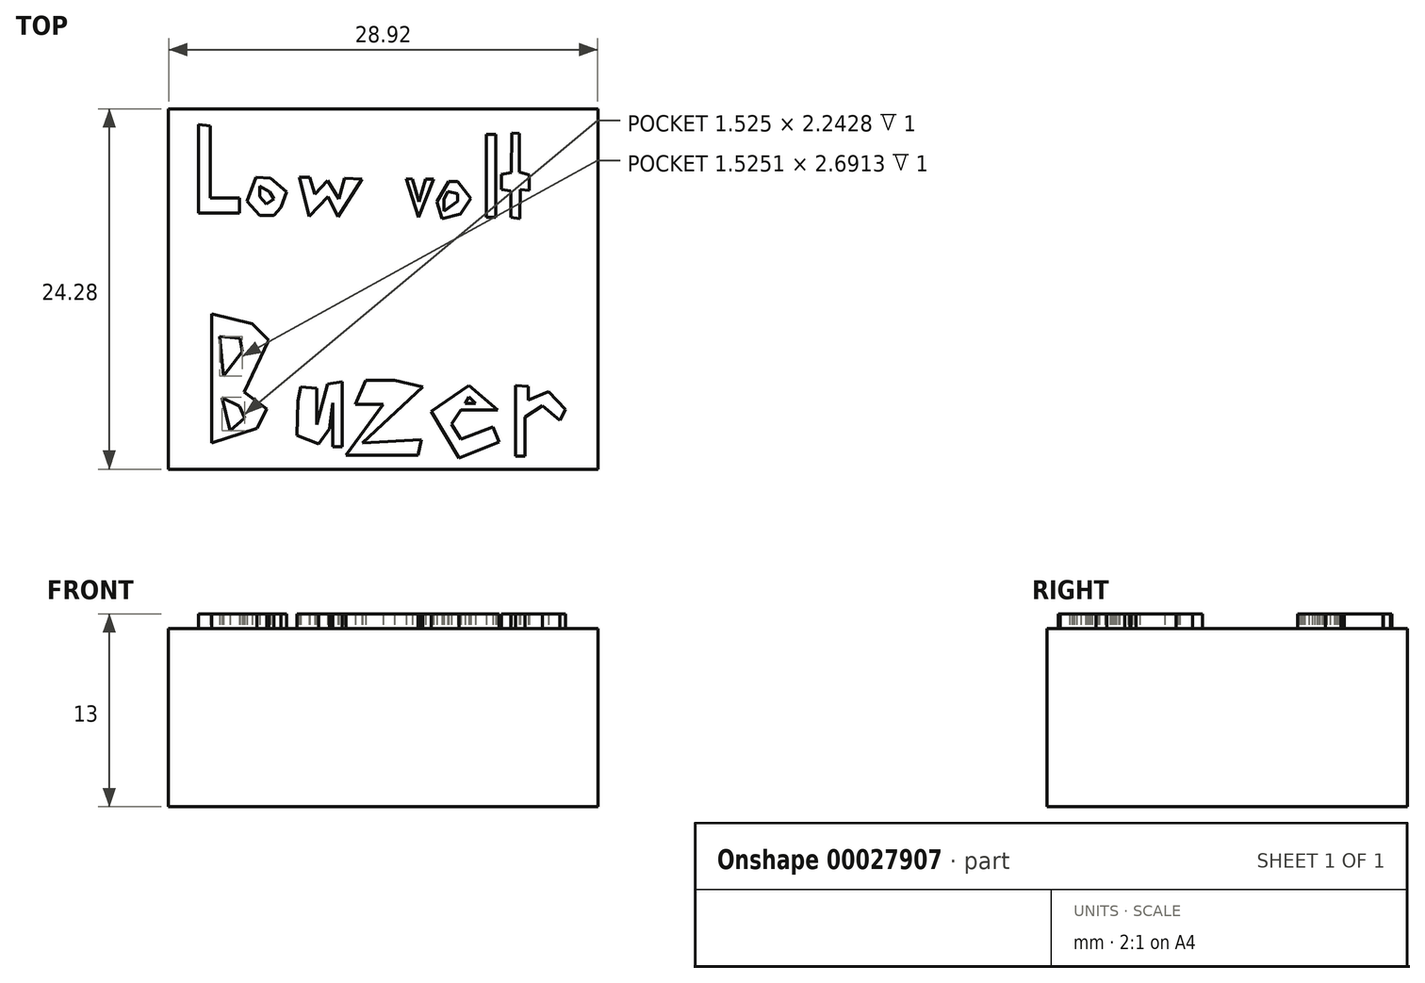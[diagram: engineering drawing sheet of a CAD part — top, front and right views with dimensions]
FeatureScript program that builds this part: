
annotation { "Feature Type Name" : "Feature", "Feature Type Description" : "" }
export const myFeature = defineFeature(function(context is Context, id is Id, definition is map)
    precondition{}
    {
        {
            var Q0;
            Q0=qCreatedBy(makeId("Top.planeOp"),FACE);
            var sketch = newSketch(context, id + "F0", { "sketchPlane" : qUnion([Q0])});
            skLineSegment(sketch, "E0.rect.bottom", {"start": v(14.47, 12.14) * mm, "end": v(-14.46, 12.14) * mm});
            skLineSegment(sketch, "E0.rect.top", {"start": v(14.47, -12.14) * mm, "end": v(-14.46, -12.14) * mm});
            skLineSegment(sketch, "E0.rect.left", {"start": v(14.47, 12.14) * mm, "end": v(14.47, -12.15) * mm});
            skLineSegment(sketch, "E0.rect.right", {"start": v(-14.46, 12.14) * mm, "end": v(-14.46, -12.14) * mm});
            skPoint(sketch, "E0.rect.middle", {"position": v(0, 0) * mm});
            skSolve(sketch);
        }
        {
            var Q0;
            Q0 = qSketchRegion(id + "F0", true);
            extrude(context, id + "F1", {"entities" : qUnion([Q0]), "depth" : 12 * mm});
        }
        {
            var Q0;
            Q0=makeQuery(id+"F1.opExtrude","CAP_FACE",FACE,{"disambiguationData":[OSD([sQuery(id+"F0.wireOp",EDGE,"E0.rect.bottom"),sQuery(id+"F0.wireOp",EDGE,"E0.rect.top"),sQuery(id+"F0.wireOp",EDGE,"E0.rect.left"),sQuery(id+"F0.wireOp",EDGE,"E0.rect.right")])],"isStart":false});
            var sketch = newSketch(context, id + "F2", { "sketchPlane" : qUnion([Q0])});
            skLineSegment(sketch, "E1", {"start": v(-12.45, 11.1) * mm, "end": v(-12.45, 5.12) * mm});
            skLineSegment(sketch, "E2", {"start": v(-12.45, 5.12) * mm, "end": v(-9.67, 5.12) * mm});
            skLineSegment(sketch, "E3", {"start": v(-9.67, 5.12) * mm, "end": v(-9.67, 6.14) * mm});
            skLineSegment(sketch, "E4", {"start": v(-9.67, 6.14) * mm, "end": v(-11.65, 6.14) * mm});
            skLineSegment(sketch, "E5", {"start": v(-11.65, 6.14) * mm, "end": v(-11.65, 11) * mm});
            skLineSegment(sketch, "E6", {"start": v(-11.65, 11) * mm, "end": v(-12.45, 11.1) * mm});
            skLineSegment(sketch, "E7", {"start": v(-8.56, 7.55) * mm, "end": v(-9.17, 5.9) * mm});
            skLineSegment(sketch, "E8", {"start": v(-9.17, 5.9) * mm, "end": v(-8.33, 4.96) * mm});
            skLineSegment(sketch, "E9", {"start": v(-8.33, 4.96) * mm, "end": v(-7.35, 4.96) * mm});
            skLineSegment(sketch, "E10", {"start": v(-7.35, 4.96) * mm, "end": v(-6.88, 5.5) * mm});
            skLineSegment(sketch, "E11", {"start": v(-6.88, 5.5) * mm, "end": v(-6.51, 6.54) * mm});
            skLineSegment(sketch, "E12", {"start": v(-6.51, 6.54) * mm, "end": v(-7.59, 7.48) * mm});
            skLineSegment(sketch, "E13", {"start": v(-7.59, 7.48) * mm, "end": v(-8.56, 7.55) * mm});
            skLineSegment(sketch, "E14", {"start": v(-8.33, 6.94) * mm, "end": v(-8.33, 6.24) * mm});
            skLineSegment(sketch, "E15", {"start": v(-8.33, 6.24) * mm, "end": v(-7.9, 5.73) * mm});
            skLineSegment(sketch, "E16", {"start": v(-7.9, 5.73) * mm, "end": v(-7.35, 6.07) * mm});
            skLineSegment(sketch, "E17", {"start": v(-7.35, 6.07) * mm, "end": v(-7.65, 6.55) * mm});
            skLineSegment(sketch, "E18", {"start": v(-7.65, 6.55) * mm, "end": v(-8.33, 6.94) * mm});
            skLineSegment(sketch, "E19", {"start": v(-5.64, 7.55) * mm, "end": v(-5, 4.9) * mm});
            skLineSegment(sketch, "E20", {"start": v(-5, 4.9) * mm, "end": v(-3.72, 6.24) * mm});
            skLineSegment(sketch, "E21", {"start": v(-3.72, 6.24) * mm, "end": v(-3.05, 4.86) * mm});
            skLineSegment(sketch, "E22", {"start": v(-3.05, 4.86) * mm, "end": v(-1.44, 7.41) * mm});
            skLineSegment(sketch, "E23", {"start": v(-1.44, 7.41) * mm, "end": v(-2.62, 7.48) * mm});
            skLineSegment(sketch, "E24", {"start": v(-2.62, 7.48) * mm, "end": v(-2.98, 6.07) * mm});
            skLineSegment(sketch, "E25", {"start": v(-2.98, 6.07) * mm, "end": v(-3.76, 7.31) * mm});
            skLineSegment(sketch, "E26", {"start": v(-3.76, 7.31) * mm, "end": v(-4.6, 6.4) * mm});
            skLineSegment(sketch, "E27", {"start": v(-4.6, 6.4) * mm, "end": v(-4.97, 7.55) * mm});
            skLineSegment(sketch, "E28", {"start": v(-4.97, 7.55) * mm, "end": v(-5.64, 7.55) * mm});
            skLineSegment(sketch, "E29", {"start": v(1.56, 7.45) * mm, "end": v(2.4, 4.84) * mm});
            skPoint(sketch, "E29.startSnap0", {"position": v(-2.03, 7.45) * mm});
            skLineSegment(sketch, "E30", {"start": v(2.4, 4.84) * mm, "end": v(3.38, 7.41) * mm});
            skLineSegment(sketch, "E31", {"start": v(3.38, 7.41) * mm, "end": v(2.84, 7.41) * mm});
            skLineSegment(sketch, "E32", {"start": v(2.84, 7.41) * mm, "end": v(2.43, 5.88) * mm});
            skLineSegment(sketch, "E33", {"start": v(2.43, 5.88) * mm, "end": v(1.98, 7.41) * mm});
            skLineSegment(sketch, "E34", {"start": v(1.98, 7.41) * mm, "end": v(1.56, 7.45) * mm});
            skLineSegment(sketch, "E35", {"start": v(4.4, 7.23) * mm, "end": v(3.62, 5.88) * mm});
            skLineSegment(sketch, "E36", {"start": v(3.62, 5.88) * mm, "end": v(3.98, 4.75) * mm});
            skLineSegment(sketch, "E37", {"start": v(3.98, 4.75) * mm, "end": v(5.2, 5.05) * mm});
            skLineSegment(sketch, "E38", {"start": v(5.2, 5.05) * mm, "end": v(5.9, 6.1) * mm});
            skLineSegment(sketch, "E39", {"start": v(5.9, 6.1) * mm, "end": v(5.03, 7.23) * mm});
            skLineSegment(sketch, "E40", {"start": v(5.03, 7.23) * mm, "end": v(4.4, 7.23) * mm});
            skLineSegment(sketch, "E41", {"start": v(4.34, 6.57) * mm, "end": v(4.1, 6.03) * mm});
            skLineSegment(sketch, "E42", {"start": v(4.1, 6.03) * mm, "end": v(4.1, 5.23) * mm});
            skLineSegment(sketch, "E43", {"start": v(4.1, 5.23) * mm, "end": v(5.03, 5.9) * mm});
            skLineSegment(sketch, "E44", {"start": v(5.03, 5.9) * mm, "end": v(5.03, 6.42) * mm});
            skLineSegment(sketch, "E45", {"start": v(5.03, 6.42) * mm, "end": v(4.34, 6.57) * mm});
            skLineSegment(sketch, "E46", {"start": v(6.95, 10.43) * mm, "end": v(6.95, 4.84) * mm});
            skLineSegment(sketch, "E47", {"start": v(6.95, 4.84) * mm, "end": v(7.57, 4.84) * mm});
            skLineSegment(sketch, "E48", {"start": v(7.57, 4.84) * mm, "end": v(7.57, 10.43) * mm});
            skLineSegment(sketch, "E49", {"start": v(7.57, 10.43) * mm, "end": v(6.95, 10.43) * mm});
            skLineSegment(sketch, "E50", {"start": v(8.6, 4.84) * mm, "end": v(8.6, 6.6) * mm});
            skLineSegment(sketch, "E51", {"start": v(8.6, 6.6) * mm, "end": v(7.96, 6.7) * mm});
            skLineSegment(sketch, "E52", {"start": v(7.96, 6.7) * mm, "end": v(7.96, 7.71) * mm});
            skLineSegment(sketch, "E53", {"start": v(7.96, 7.71) * mm, "end": v(8.65, 7.86) * mm});
            skLineSegment(sketch, "E54", {"start": v(8.65, 7.86) * mm, "end": v(8.68, 10.52) * mm});
            skLineSegment(sketch, "E55", {"start": v(8.68, 10.52) * mm, "end": v(9.2, 10.5) * mm});
            skLineSegment(sketch, "E56", {"start": v(9.2, 10.5) * mm, "end": v(9.16, 7.9) * mm});
            skLineSegment(sketch, "E57", {"start": v(9.16, 7.9) * mm, "end": v(9.85, 7.68) * mm});
            skLineSegment(sketch, "E58", {"start": v(9.85, 7.68) * mm, "end": v(9.85, 6.63) * mm});
            skLineSegment(sketch, "E59", {"start": v(9.85, 6.63) * mm, "end": v(9.25, 6.72) * mm});
            skLineSegment(sketch, "E60", {"start": v(9.25, 6.72) * mm, "end": v(9.22, 4.75) * mm});
            skLineSegment(sketch, "E61", {"start": v(9.22, 4.75) * mm, "end": v(8.6, 4.84) * mm});
            skLineSegment(sketch, "E62", {"start": v(-11.57, -1.66) * mm, "end": v(-11.57, -10.36) * mm});
            skLineSegment(sketch, "E63", {"start": v(-11.57, -10.36) * mm, "end": v(-8.52, -9.37) * mm});
            skLineSegment(sketch, "E64", {"start": v(-8.52, -9.37) * mm, "end": v(-7.85, -8.07) * mm});
            skLineSegment(sketch, "E65", {"start": v(-7.85, -8.07) * mm, "end": v(-9.37, -6.95) * mm});
            skLineSegment(sketch, "E66", {"start": v(-9.37, -6.95) * mm, "end": v(-7.71, -3.45) * mm});
            skLineSegment(sketch, "E67", {"start": v(-7.71, -3.45) * mm, "end": v(-8.83, -2.33) * mm});
            skLineSegment(sketch, "E68", {"start": v(-8.83, -2.33) * mm, "end": v(-11.57, -1.66) * mm});
            skLineSegment(sketch, "E69", {"start": v(-11.03, -3.18) * mm, "end": v(-10.76, -5.88) * mm});
            skLineSegment(sketch, "E70", {"start": v(-10.76, -5.88) * mm, "end": v(-9.5, -4.22) * mm});
            skLineSegment(sketch, "E71", {"start": v(-9.5, -4.22) * mm, "end": v(-9.64, -3.32) * mm});
            skLineSegment(sketch, "E72", {"start": v(-9.64, -3.32) * mm, "end": v(-11.03, -3.18) * mm});
            skLineSegment(sketch, "E73", {"start": v(-10.85, -7.31) * mm, "end": v(-9.68, -7.9) * mm});
            skLineSegment(sketch, "E74", {"start": v(-9.68, -7.9) * mm, "end": v(-9.33, -8.7) * mm});
            skLineSegment(sketch, "E75", {"start": v(-9.33, -8.7) * mm, "end": v(-10.31, -9.55) * mm});
            skLineSegment(sketch, "E76", {"start": v(-10.31, -9.55) * mm, "end": v(-10.85, -7.31) * mm});
            skLineSegment(sketch, "E77", {"start": v(-5.56, -6.6) * mm, "end": v(-5.74, -7.54) * mm});
            skLineSegment(sketch, "E78", {"start": v(-5.83, -9.87) * mm, "end": v(-5.74, -7.54) * mm});
            skLineSegment(sketch, "E79", {"start": v(-5.83, -9.87) * mm, "end": v(-4.35, -10.45) * mm});
            skLineSegment(sketch, "E80", {"start": v(-4.35, -10.45) * mm, "end": v(-3.63, -9.42) * mm});
            skLineSegment(sketch, "E81", {"start": v(-3.63, -9.42) * mm, "end": v(-3.4, -7.67) * mm});
            skLineSegment(sketch, "E82", {"start": v(-3.4, -7.67) * mm, "end": v(-3.4, -10.63) * mm});
            skLineSegment(sketch, "E83", {"start": v(-3.4, -10.63) * mm, "end": v(-2.78, -10.63) * mm});
            skLineSegment(sketch, "E84", {"start": v(-2.78, -10.63) * mm, "end": v(-2.78, -6.24) * mm});
            skLineSegment(sketch, "E85", {"start": v(-2.78, -6.24) * mm, "end": v(-3.76, -6.41) * mm});
            skLineSegment(sketch, "E86", {"start": v(-3.76, -6.41) * mm, "end": v(-4.48, -9.15) * mm});
            skLineSegment(sketch, "E87", {"start": v(-4.48, -9.15) * mm, "end": v(-4.48, -6.68) * mm});
            skLineSegment(sketch, "E88", {"start": v(-4.48, -6.68) * mm, "end": v(-5.56, -6.6) * mm});
            skLineSegment(sketch, "E89", {"start": v(-1.16, -6.15) * mm, "end": v(0.77, -6.15) * mm});
            skLineSegment(sketch, "E90", {"start": v(2.65, -6.6) * mm, "end": v(-1.39, -10.36) * mm});
            skLineSegment(sketch, "E91", {"start": v(-1.39, -10.36) * mm, "end": v(2.56, -10.14) * mm});
            skLineSegment(sketch, "E92", {"start": v(2.56, -10.14) * mm, "end": v(2.34, -11.21) * mm});
            skLineSegment(sketch, "E93", {"start": v(2.34, -11.21) * mm, "end": v(-2.5, -11.21) * mm});
            skLineSegment(sketch, "E94", {"start": v(-2.5, -11.21) * mm, "end": v(0, -7.76) * mm});
            skLineSegment(sketch, "E95", {"start": v(0, -7.76) * mm, "end": v(-1.88, -7.76) * mm});
            skLineSegment(sketch, "E96", {"start": v(-1.88, -7.76) * mm, "end": v(-1.16, -6.15) * mm});
            skLineSegment(sketch, "E97", {"start": v(0.77, -6.15) * mm, "end": v(2.65, -6.6) * mm});
            skLineSegment(sketch, "E98", {"start": v(5.25, -8.16) * mm, "end": v(7.72, -8.16) * mm});
            skLineSegment(sketch, "E99", {"start": v(7.72, -8.16) * mm, "end": v(5.8, -6.5) * mm});
            skLineSegment(sketch, "E100", {"start": v(5.8, -6.5) * mm, "end": v(3.23, -8.25) * mm});
            skLineSegment(sketch, "E101", {"start": v(3.23, -8.25) * mm, "end": v(5.12, -11.4) * mm});
            skLineSegment(sketch, "E102", {"start": v(5.12, -11.4) * mm, "end": v(7.8, -10.32) * mm});
            skLineSegment(sketch, "E103", {"start": v(7.8, -10.32) * mm, "end": v(7.4, -9.29) * mm});
            skLineSegment(sketch, "E104", {"start": v(7.4, -9.29) * mm, "end": v(5.24, -10.13) * mm});
            skLineSegment(sketch, "E105", {"start": v(5.24, -10.13) * mm, "end": v(4.62, -9.1) * mm});
            skLineSegment(sketch, "E106", {"start": v(4.62, -9.1) * mm, "end": v(5.25, -8.16) * mm});
            skLineSegment(sketch, "E107", {"start": v(5.52, -7.72) * mm, "end": v(6.24, -7.72) * mm});
            skLineSegment(sketch, "E108", {"start": v(6.24, -7.72) * mm, "end": v(5.8, -7.27) * mm});
            skLineSegment(sketch, "E109", {"start": v(5.8, -7.27) * mm, "end": v(5.52, -7.72) * mm});
            skLineSegment(sketch, "E110", {"start": v(8.93, -6.5) * mm, "end": v(8.93, -11.26) * mm});
            skLineSegment(sketch, "E111", {"start": v(8.93, -11.26) * mm, "end": v(9.56, -11.26) * mm});
            skLineSegment(sketch, "E112", {"start": v(9.56, -11.26) * mm, "end": v(9.56, -8.61) * mm});
            skLineSegment(sketch, "E113", {"start": v(9.56, -8.61) * mm, "end": v(10.72, -7.85) * mm});
            skLineSegment(sketch, "E114", {"start": v(10.72, -7.85) * mm, "end": v(11.9, -8.84) * mm});
            skLineSegment(sketch, "E115", {"start": v(11.9, -8.84) * mm, "end": v(12.3, -8.12) * mm});
            skLineSegment(sketch, "E116", {"start": v(12.3, -8.12) * mm, "end": v(11.13, -6.9) * mm});
            skLineSegment(sketch, "E117", {"start": v(11.13, -6.9) * mm, "end": v(9.78, -7.5) * mm});
            skLineSegment(sketch, "E118", {"start": v(9.78, -7.5) * mm, "end": v(9.78, -6.55) * mm});
            skLineSegment(sketch, "E119", {"start": v(9.78, -6.55) * mm, "end": v(8.93, -6.5) * mm});
            skSolve(sketch);
        }
        {
            var Q0;
            Q0 = qSketchRegion(id + "F2", true);
            extrude(context, id + "F3", {"entities" : qUnion([Q0]), "operationType" : NewBodyOperationType.ADD, "depth" : 1 * mm});
        }
    });
